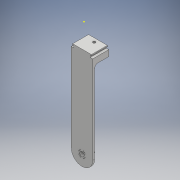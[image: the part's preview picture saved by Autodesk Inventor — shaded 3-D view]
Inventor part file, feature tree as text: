
AUTODESK INVENTOR PART (.ipt)
format: ipt  version: 2018 (Build 220112000, 112)  size: 216,576 bytes
history: native  units: mm
features: sketch x5, extrude x3, projected_geometry x3, hole x1, fillet x1
ambient origin geometry x8: Origin, YZ Plane, XZ Plane, XY Plane, X Axis, Y Axis, Z Axis, Center Point
bodies: Solid1 (feature_tree)
feature tree (13):
  extrude  "Extrusion1"  Depth=300.0mm
  extrude  "Extrusion2"  Depth=5.0mm TaperAngle=0.0deg
  sketch  "Sketch3"  dims[d5=16.0mm d6=37.0mm d7=0.0mm]
  extrude  "Extrusion3"  Depth=37.0mm TaperAngle=0.0deg
  hole  "Hole1"  [1 undecoded]
  fillet  "Fillet1"  Radius=10.0mm
  sketch  "Sketch1"  dims[d0=300.0mm d1=0.3mm]
  sketch  "Sketch2"  dims[d2=150.0mm d3=5.0mm d4=0.0mm]
  projected_geometry  "Projected Loop1"
  sketch  "Sketch4"  dims[d8=26.0mm d9=15.5mm d10=0.0mm d11=10.0mm]
  projected_geometry  "Projected Loop2"
  sketch  "Sketch5"  dims[d12=7.0mm d13=6.0mm d14=11.0mm d15=8.0mm d16=90.0deg d17=8.0mm d18=20.594885mm d19=8.0mm]
  projected_geometry  "Projected Loop3"
note: 1 required parameter value undecoded (feature->parameter linkage not recoverable at this tier; creation-order binding heuristic only, values carry confidence <= 0.55)
